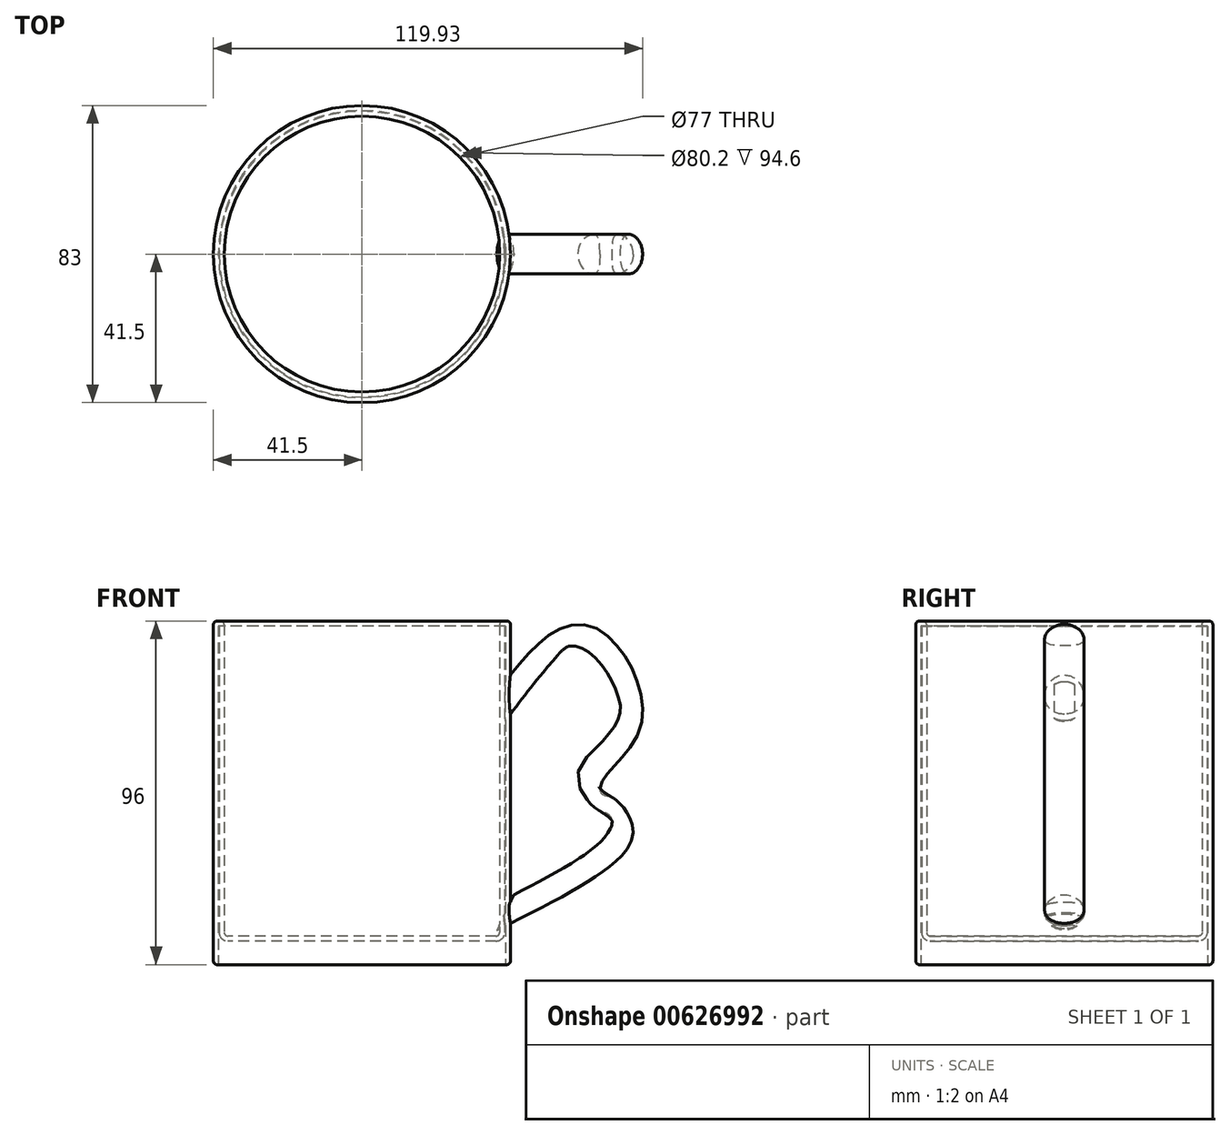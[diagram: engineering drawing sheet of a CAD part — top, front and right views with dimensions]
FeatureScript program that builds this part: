
annotation { "Feature Type Name" : "Feature", "Feature Type Description" : "" }
export const myFeature = defineFeature(function(context is Context, id is Id, definition is map)
    precondition{}
    {
        {
            var Q0;
            Q0=qCreatedBy(makeId("Top.planeOp"),FACE);
            var sketch = newSketch(context, id + "F0", { "sketchPlane" : qUnion([Q0])});
            skCircle(sketch, "E0", {"center": v(0, 0) * mm, "radius": 41.5 * mm});
            skSolve(sketch);
        }
        {
            var Q0;
            Q0 = qSketchRegion(id + "F0", true);
            extrude(context, id + "F1", {"entities" : qUnion([Q0]), "depth" : 96 * mm, "offsetDistance" : 25 * mm});
        }
        {
            var Q0;
            Q0=qCreatedBy(makeId("Right.planeOp"),FACE);
            cPlane(context, id + "F2", {"entities" : qUnion([Q0]), "cplaneType" : CPlaneType.OFFSET, "offset" : 40 * mm, "width" : 150 * mm, "height" : 150 * mm});
        }
        {
            var Q0;
            Q0=makeQuery(id+"F1.opExtrude","CAP_FACE",FACE,{"disambiguationData":[OSD([sQuery(id+"F0.wireOp",EDGE,"E0")])],"isStart":false});
            shell(context, id + "F3", {"entities" : qUnion([Q0]), "thickness" : 3 * mm});
        }
        {
            var Q0;
            Q0=makeQuery(id+"F1.opExtrude","CAP_EDGE",EDGE,{"disambiguationData":[OSD([sQuery(id+"F0.wireOp",EDGE,"E0")])],"isStart":false});
            fillet(context, id + "F4", {"entities" : qUnion([Q0]), "radius" : 1 * mm, "tangentPropagation" : true, "allowEdgeOverflow" : false});
        }
        {
            var Q0;
            {var subQ0=sQuery(id+"F0.wireOp",EDGE,"E0");Q0=makeQuery(id+"F3.opShell","OFFSET_EDGE",EDGE,{"disambiguationData":[OSD([subQ0]),TDD([makeQuery(id+"F1.opExtrude","CAP_EDGE",EDGE,{"disambiguationData":[OSD([subQ0])],"isStart":false})])]});}
            fillet(context, id + "F5", {"entities" : qUnion([Q0]), "radius" : 1 * mm, "tangentPropagation" : true, "allowEdgeOverflow" : false});
        }
        {
            var Q0;
            Q0=makeQuery(id+"F1.opExtrude","CAP_EDGE",EDGE,{"disambiguationData":[OSD([sQuery(id+"F0.wireOp",EDGE,"E0")])],"isStart":true});
            fillet(context, id + "F6", {"entities" : qUnion([Q0]), "radius" : 1 * mm, "tangentPropagation" : true, "allowEdgeOverflow" : false});
        }
        {
            var Q0;
            {var subQ0=sQuery(id+"F0.wireOp",EDGE,"E0");Q0=makeQuery(id+"F3.opShell","OFFSET_FACE",FACE,{"disambiguationData":[OSD([subQ0]),TDD([makeQuery(id+"F1.opExtrude","CAP_FACE",FACE,{"disambiguationData":[OSD([subQ0])],"isStart":true})])]});}
            extrude(context, id + "F7", {"entities" : qUnion([Q0]), "operationType" : NewBodyOperationType.ADD, "depth" : 5 * mm, "offsetDistance" : 25 * mm});
        }
        {
            var Q0;
            Q0=makeQuery(id+"F7.opExtrude","CAP_FACE",FACE,{"disambiguationData":[OSD([sQuery(id+"F0.wireOp",EDGE,"E0")])],"isStart":false});
            fillet(context, id + "F8", {"entities" : qUnion([Q0]), "radius" : 1 * mm, "tangentPropagation" : true, "allowEdgeOverflow" : false});
        }
        {
            var Q0;
            Q0=makeQuery(id+"F1.opExtrude","CAP_FACE",FACE,{"disambiguationData":[OSD([sQuery(id+"F0.wireOp",EDGE,"E0")])],"isStart":true});
            shell(context, id + "F9", {"entities" : qUnion([Q0]), "thickness" : 1.4 * mm});
        }
        {
            var Q0;
            Q0=qCreatedBy(id+"F2.planeOp",FACE);
            var sketch = newSketch(context, id + "F10", { "sketchPlane" : qUnion([Q0])});
            skCircle(sketch, "E1", {"center": v(0, 73.5) * mm, "radius": 5.5 * mm});
            skSolve(sketch);
        }
        {
            var Q0;
            Q0=qCreatedBy(makeId("Front.planeOp"),FACE);
            var sketch = newSketch(context, id + "F11", { "sketchPlane" : qUnion([Q0])});
            skFitSpline(sketch, "E2", {"points": [v(40.03, 73.64) * mm, v(62.1, 90.86) * mm, v(74.46, 68.58) * mm, v(64.74, 51.36) * mm, v(71.63, 38.19) * mm, v(40.03, 14.49) * mm], "startDerivative": vector(103.92, 134.45) * mm, "endDerivative": vector(-190.74, -96.58) * mm});
            skSolve(sketch);
        }
        {
            var Q0;
            Q0 = qSketchRegion(id + "F10", true);
            var Q1;
            Q1=sQuery(id+"F11.wireOp",EDGE,"E2");
            sweep(context, id + "F12", {"operationType" : NewBodyOperationType.ADD, "profiles" : qUnion([Q0]), "path" : qUnion([Q1])});
        }
    });
